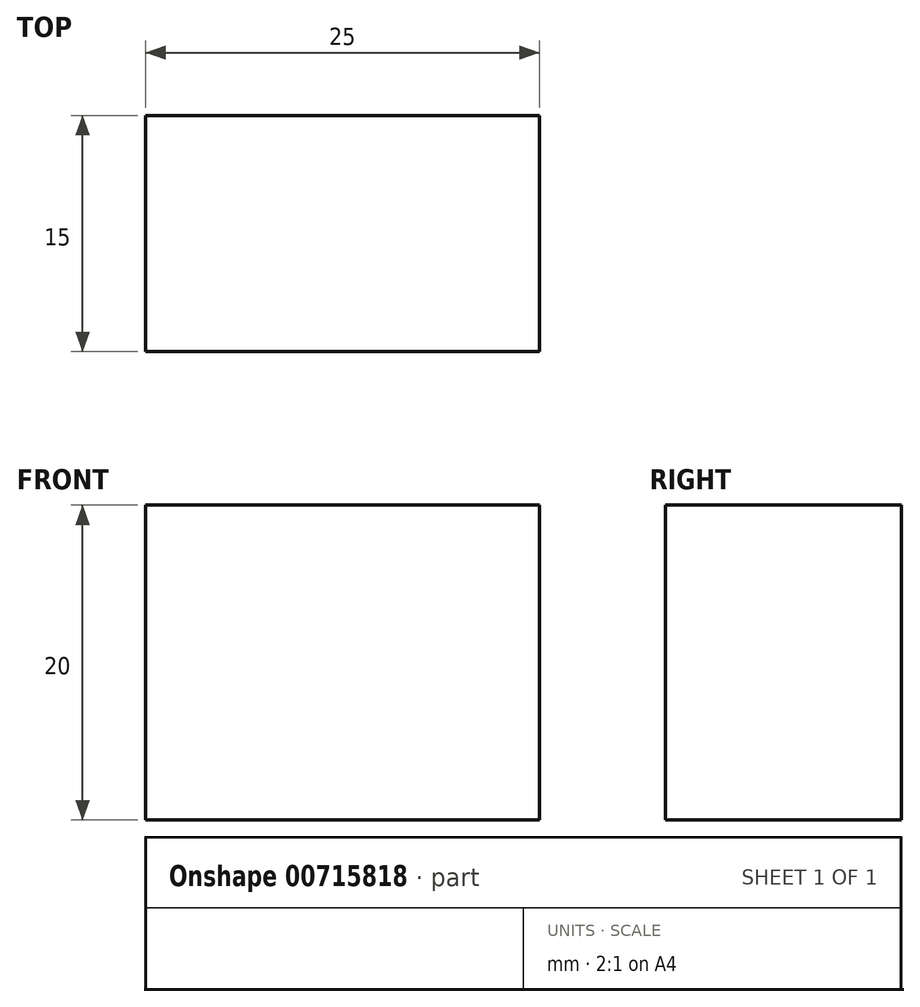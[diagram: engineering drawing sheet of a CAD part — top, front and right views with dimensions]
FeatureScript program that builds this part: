
annotation { "Feature Type Name" : "Feature", "Feature Type Description" : "" }
export const myFeature = defineFeature(function(context is Context, id is Id, definition is map)
    precondition{}
    {
        {
            var Q0;
            Q0=qCreatedBy(makeId("Right.planeOp"),FACE);
            var sketch = newSketch(context, id + "F0", { "sketchPlane" : qUnion([Q0])});
            skLineSegment(sketch, "E0.bottom", {"start": v(-19.23, -15.2) * mm, "end": v(-4.23, -15.2) * mm});
            skLineSegment(sketch, "E0.top", {"start": v(-19.23, -35.2) * mm, "end": v(-4.23, -35.2) * mm});
            skLineSegment(sketch, "E0.left", {"start": v(-19.23, -15.2) * mm, "end": v(-19.23, -35.2) * mm});
            skLineSegment(sketch, "E0.right", {"start": v(-4.23, -15.2) * mm, "end": v(-4.23, -35.2) * mm});
            skSolve(sketch);
        }
        {
            var Q0;
            Q0 = qSketchRegion(id + "F0", true);
            extrude(context, id + "F1", {"entities" : qUnion([Q0]), "depth" : 25 * mm, "offsetDistance" : 25 * mm});
        }
    });
